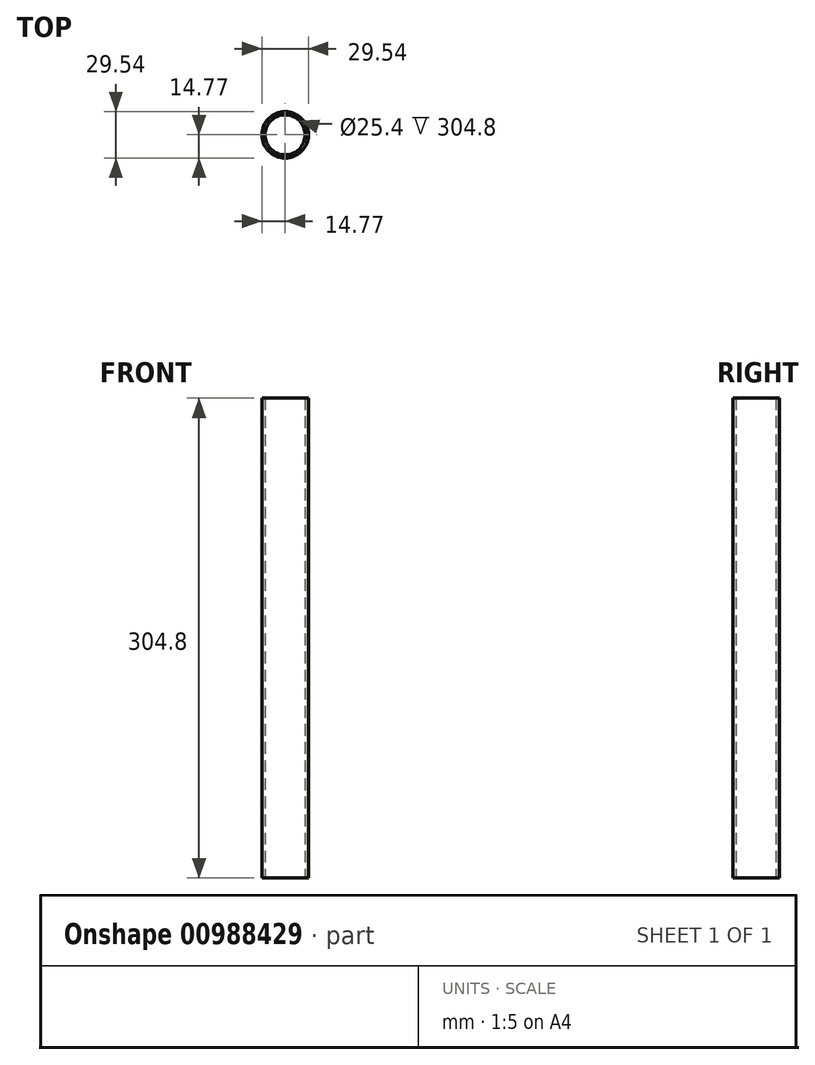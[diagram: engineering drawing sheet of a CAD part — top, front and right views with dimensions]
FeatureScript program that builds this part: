
annotation { "Feature Type Name" : "Feature", "Feature Type Description" : "" }
export const myFeature = defineFeature(function(context is Context, id is Id, definition is map)
    precondition{}
    {
        {
            assignVariable(context, id + "F0", {"name" : "RodLength", "anyValue" : 304.8 * mm});
        }
        {
            var Q0;
            Q0=qCreatedBy(makeId("Top.planeOp"),FACE);
            var sketch = newSketch(context, id + "F1", { "sketchPlane" : qUnion([Q0])});
            skCircle(sketch, "E0", {"center": v(0, 0) * mm, "radius": 12.7 * mm});
            skCircle(sketch, "E1", {"center": v(0, 0) * mm, "radius": 14.77 * mm});
            skSolve(sketch);
        }
        {
            var Q0;
            Q0=makeQuery(id+"F1.imprint","IMPRINT",FACE,{"disambiguationData":[TD([[makeQuery(id+"F1.imprint","IMPRINT",EDGE,{"derivedFrom":sQuery(id+"F1.wireOp",EDGE,"E0")}),-1.0]])]});
            extrude(context, id + "F2", {"entities" : qUnion([Q0]), "depth" : getVariable(context, 'RodLength'), "offsetDistance" : 25.4 * mm});
        }
    });
